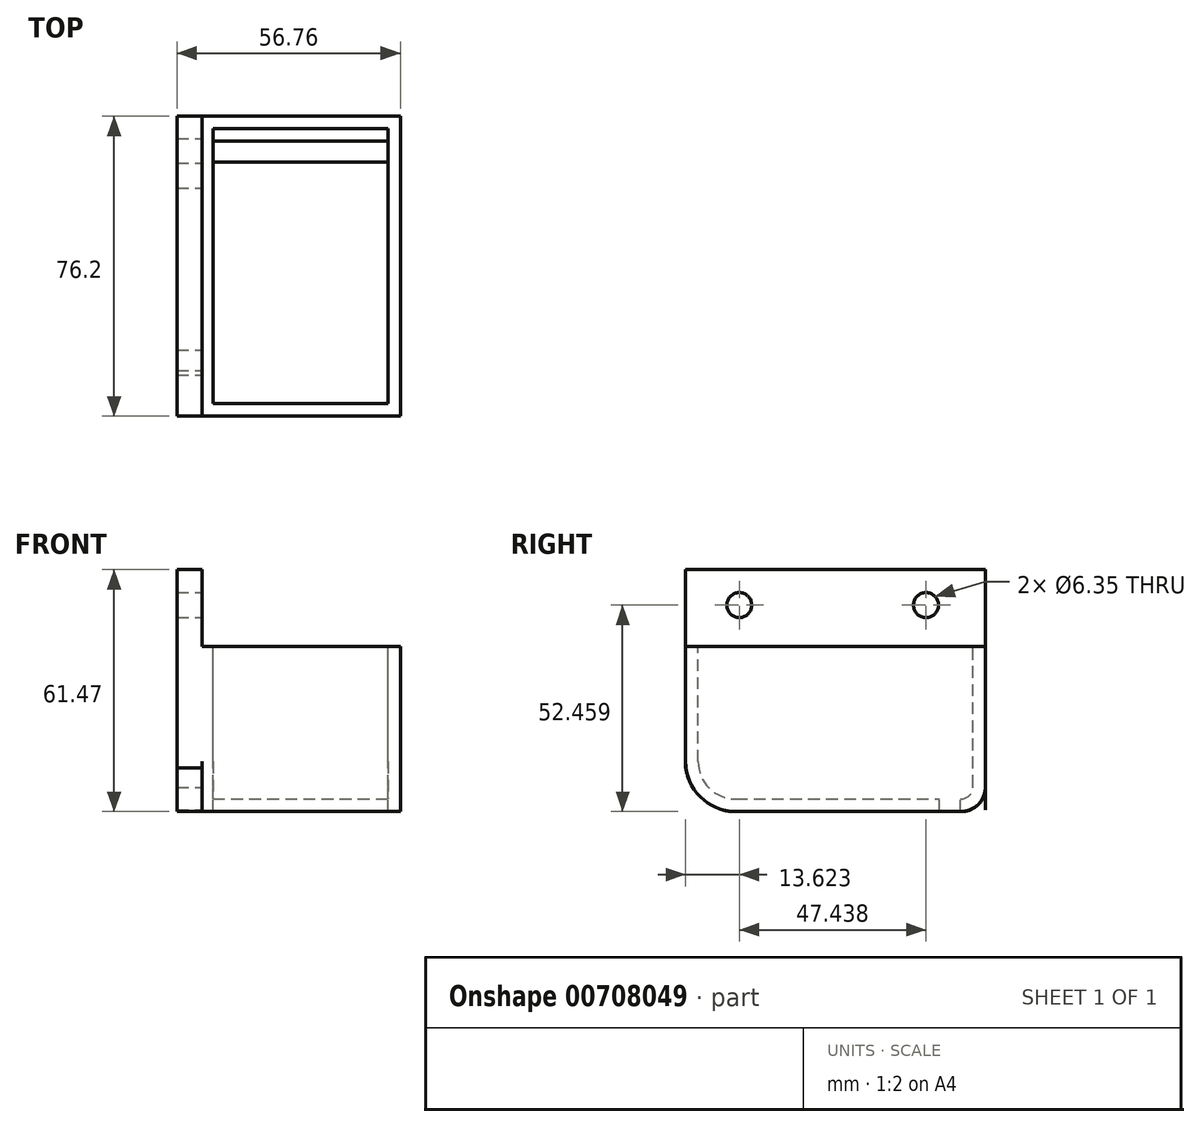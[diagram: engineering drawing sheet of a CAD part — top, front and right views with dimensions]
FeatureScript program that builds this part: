
annotation { "Feature Type Name" : "Feature", "Feature Type Description" : "" }
export const myFeature = defineFeature(function(context is Context, id is Id, definition is map)
    precondition{}
    {
        {
            var Q0;
            Q0=qCreatedBy(makeId("Right.planeOp"),FACE);
            var sketch = newSketch(context, id + "F0", { "sketchPlane" : qUnion([Q0])});
            skLineSegment(sketch, "E0.bottom", {"start": v(12.7, 0) * mm, "end": v(69.85, 0) * mm});
            skLineSegment(sketch, "E0.top", {"start": v(0, 41.91) * mm, "end": v(76.2, 41.91) * mm});
            skLineSegment(sketch, "E0.left", {"start": v(0, 12.7) * mm, "end": v(0, 41.91) * mm});
            skLineSegment(sketch, "E0.right", {"start": v(76.2, 6.35) * mm, "end": v(76.2, 41.91) * mm});
            skPoint(sketch, "E1.visualSharp", {"position": v(0, 0) * mm});
            skArc(sketch, "E1.filletArc", {"start": v(0, 12.7) * mm, "mid": v(3.72, 3.72) * mm, "end": v(12.7, 0) * mm});
            skPoint(sketch, "E2.visualSharp", {"position": v(76.2, 0) * mm});
            skArc(sketch, "E2.filletArc", {"start": v(69.85, 0) * mm, "mid": v(74.34, 1.86) * mm, "end": v(76.2, 6.35) * mm});
            skSolve(sketch);
        }
        {
            var Q0;
            Q0=makeQuery(id+"F0.imprint","IMPRINT",FACE,{"disambiguationData":[TD([[makeQuery(id+"F0.imprint","IMPRINT",EDGE,{"derivedFrom":sQuery(id+"F0.wireOp",EDGE,"E0.bottom")}),1.0]])]});
            extrude(context, id + "F1", {"entities" : qUnion([Q0]), "depth" : 50.8 * mm, "offsetDistance" : 25.4 * mm});
        }
        {
            var Q0;
            Q0=makeQuery(id+"F1.opExtrude","SWEPT_FACE",FACE,{"disambiguationData":[OSD([sQuery(id+"F0.wireOp",EDGE,"E0.top")])]});
            shell(context, id + "F2", {"entities" : qUnion([Q0]), "thickness" : 3.17 * mm});
        }
        {
            var Q0;
            Q0=makeQuery(id+"F2.opShell","OFFSET_FACE",FACE,{"disambiguationData":[OSD([sQuery(id+"F0.wireOp",EDGE,"E0.bottom")])]});
            var sketch = newSketch(context, id + "F3", { "sketchPlane" : qUnion([Q0])});
            skLineSegment(sketch, "E3.bottom", {"start": v(3.17, 69.85) * mm, "end": v(47.63, 69.85) * mm});
            skLineSegment(sketch, "E3.top", {"start": v(3.17, 64.51) * mm, "end": v(47.63, 64.51) * mm});
            skLineSegment(sketch, "E3.left", {"start": v(3.17, 69.85) * mm, "end": v(3.17, 64.51) * mm});
            skLineSegment(sketch, "E3.right", {"start": v(47.63, 69.85) * mm, "end": v(47.63, 64.51) * mm});
            skSolve(sketch);
        }
        {
            var Q0;
            Q0=makeQuery(id+"F3.imprint","IMPRINT",FACE,{"disambiguationData":[TD([[makeQuery(id+"F3.imprint","IMPRINT",EDGE,{"derivedFrom":sQuery(id+"F3.wireOp",EDGE,"E3.bottom")}),1.0]])]});
            extrude(context, id + "F4", {"entities" : qUnion([Q0]), "operationType" : NewBodyOperationType.REMOVE, "oppositeDirection" : true, "depth" : 25.4 * mm, "offsetDistance" : 25.4 * mm});
        }
        {
            var Q0;
            Q0=qCreatedBy(makeId("Top.planeOp"),FACE);
            var sketch = newSketch(context, id + "F5", { "sketchPlane" : qUnion([Q0])});
            skLineSegment(sketch, "E4.bottom", {"start": v(0.4, 0) * mm, "end": v(-5.96, 0) * mm});
            skLineSegment(sketch, "E4.top", {"start": v(0.4, 76.2) * mm, "end": v(-5.96, 76.2) * mm});
            skLineSegment(sketch, "E4.left", {"start": v(0.4, 0) * mm, "end": v(0.4, 76.2) * mm});
            skLineSegment(sketch, "E4.right", {"start": v(-5.96, 0) * mm, "end": v(-5.96, 76.2) * mm});
            skSolve(sketch);
        }
        {
            var Q0;
            Q0=makeQuery(id+"F5.imprint","IMPRINT",FACE,{"disambiguationData":[TD([[makeQuery(id+"F5.imprint","IMPRINT",EDGE,{"derivedFrom":sQuery(id+"F5.wireOp",EDGE,"E4.bottom")}),-1.0]])]});
            extrude(context, id + "F6", {"entities" : qUnion([Q0]), "operationType" : NewBodyOperationType.ADD, "depth" : 61.47 * mm, "offsetDistance" : 25.4 * mm});
        }
        {
            var Q0;
            {var subQ1=sQuery(id+"F5.wireOp",EDGE,"E4.left");Q0=makeQuery(id+"F6.boolean.opBoolean","SPLIT",FACE,{"disambiguationData":[TD([makeQuery(id+"F1.opExtrude","SWEPT_FACE",FACE,{"disambiguationData":[OSD([sQuery(id+"F0.wireOp",EDGE,"E0.top")])]})])],"derivedFrom":makeQuery(id+"F6.opExtrude","SWEPT_FACE",FACE,{"disambiguationData":[OSD([subQ1])]})});}
            var sketch = newSketch(context, id + "F7", { "sketchPlane" : qUnion([Q0])});
            skArc(sketch, "E5", {"start": v(0, 11.12) * mm, "mid": v(3.88, 3.6) * mm, "end": v(11.54, 0) * mm});
            skLineSegment(sketch, "E6", {"start": v(11.54, 0) * mm, "end": v(0, 0) * mm});
            skLineSegment(sketch, "E7", {"start": v(0, 0) * mm, "end": v(0, 11.12) * mm});
            skCircle(sketch, "E8", {"center": v(13.62, 52.46) * mm, "radius": 3.18 * mm});
            skCircle(sketch, "E9", {"center": v(61.06, 52.46) * mm, "radius": 3.18 * mm});
            skPoint(sketch, "E10.end.orphan", {"position": v(70.5, 0) * mm});
            skPoint(sketch, "E10.start.orphan", {"position": v(76.03, 0) * mm});
            skArc(sketch, "E11", {"start": v(70.5, 0) * mm, "mid": v(74.53, 1.97) * mm, "end": v(76.18, 6.14) * mm});
            skLineSegment(sketch, "E12", {"start": v(76.18, 6.14) * mm, "end": v(76.2, 0) * mm});
            skLineSegment(sketch, "E13", {"start": v(76.2, 0) * mm, "end": v(70.5, 0) * mm});
            skSolve(sketch);
        }
        {
            var Q0;
            Q0=makeQuery(id+"F7.imprint","IMPRINT",FACE,{"disambiguationData":[TD([[makeQuery(id+"F7.imprint","IMPRINT",EDGE,{"derivedFrom":sQuery(id+"F7.wireOp",EDGE,"E8")}),1.0]])]});
            var Q1;
            Q1=makeQuery(id+"F7.imprint","IMPRINT",FACE,{"disambiguationData":[TD([[makeQuery(id+"F7.imprint","IMPRINT",EDGE,{"derivedFrom":sQuery(id+"F7.wireOp",EDGE,"E9")}),1.0]])]});
            var Q2;
            Q2=makeQuery(id+"F7.imprint","IMPRINT",FACE,{"disambiguationData":[TD([[makeQuery(id+"F7.imprint","IMPRINT",EDGE,{"derivedFrom":sQuery(id+"F7.wireOp",EDGE,"meqcgFQN-2I3f-cbvm-i51j-zUAFHZP41aOU")}),-1.0]])]});
            var Q3;
            Q3=makeQuery(id+"F7.imprint","IMPRINT",FACE,{"disambiguationData":[TD([[makeQuery(id+"F7.imprint","IMPRINT",EDGE,{"derivedFrom":sQuery(id+"F7.wireOp",EDGE,"E5")}),-1.0]])]});
            var Q4;
            Q4=makeQuery(id+"F7.imprint","IMPRINT",FACE,{"disambiguationData":[TD([[makeQuery(id+"F7.imprint","IMPRINT",EDGE,{"derivedFrom":sQuery(id+"F7.wireOp",EDGE,"E11")}),-1.0]])]});
            extrude(context, id + "F8", {"entities" : qUnion([Q0, Q1, Q2, Q3, Q4]), "operationType" : NewBodyOperationType.REMOVE, "oppositeDirection" : true, "depth" : 25.4 * mm, "offsetDistance" : 25.4 * mm});
        }
    });
